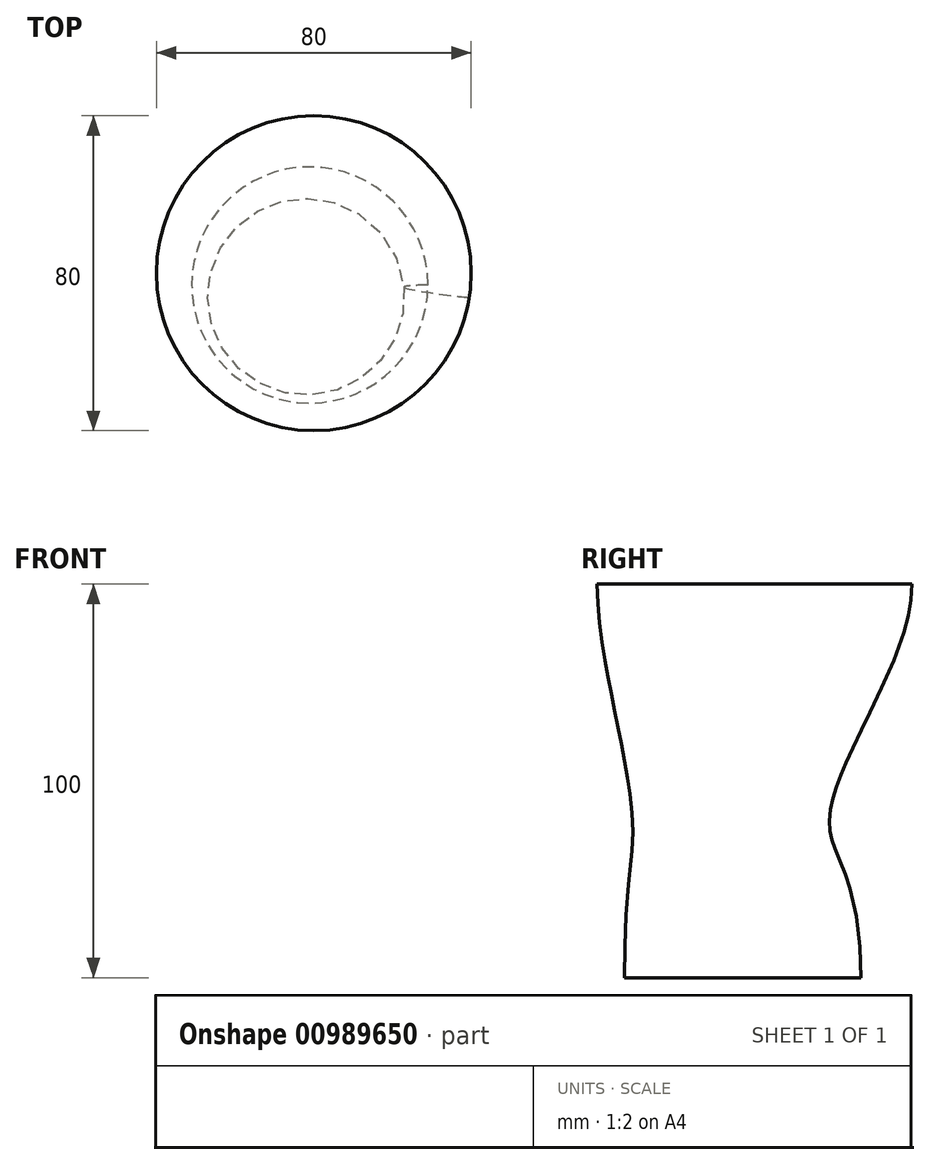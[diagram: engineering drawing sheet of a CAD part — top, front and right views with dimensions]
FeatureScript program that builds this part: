
annotation { "Feature Type Name" : "Feature", "Feature Type Description" : "" }
export const myFeature = defineFeature(function(context is Context, id is Id, definition is map)
    precondition{}
    {
        {
            assignVariable(context, id + "F0", {"name" : "Hossz", "anyValue" : 100});
        }
        {
            var Q0;
            Q0=qCreatedBy(makeId("Top.planeOp"),FACE);
            cPlane(context, id + "F1", {"entities" : qUnion([Q0]), "cplaneType" : CPlaneType.OFFSET, "offset" : (getVariable(context, 'Hossz')) * mm, "width" : 150 * mm, "height" : 150 * mm});
        }
        {
            var Q0;
            Q0=qCreatedBy(makeId("Top.planeOp"),FACE);
            cPlane(context, id + "F2", {"entities" : qUnion([Q0]), "cplaneType" : CPlaneType.OFFSET, "offset" : 40 * mm, "width" : 150 * mm, "height" : 150 * mm});
        }
        {
            var Q0;
            Q0=qCreatedBy(makeId("Top.planeOp"),FACE);
            var sketch = newSketch(context, id + "F3", { "sketchPlane" : qUnion([Q0])});
            skCircle(sketch, "E0", {"center": v(0, 0) * mm, "radius": 30 * mm});
            skSolve(sketch);
        }
        {
            var Q0;
            Q0=qCreatedBy(id+"F2.planeOp",FACE);
            var sketch = newSketch(context, id + "F4", { "sketchPlane" : qUnion([Q0])});
            skCircle(sketch, "E1", {"center": v(-1, -3) * mm, "radius": 25 * mm});
            skSolve(sketch);
        }
        {
            var Q0;
            Q0=qCreatedBy(id+"F1.planeOp",FACE);
            var sketch = newSketch(context, id + "F5", { "sketchPlane" : qUnion([Q0])});
            skCircle(sketch, "E2", {"center": v(1, 3) * mm, "radius": 40 * mm});
            skSolve(sketch);
        }
        {
            var Q0;
            Q0=makeQuery(id+"F3.imprint","IMPRINT",FACE,{"disambiguationData":[TD([[makeQuery(id+"F3.imprint","IMPRINT",EDGE,{"derivedFrom":sQuery(id+"F3.wireOp",EDGE,"E0")}),1.0]])]});
            var Q1;
            Q1=makeQuery(id+"F4.imprint","IMPRINT",FACE,{"disambiguationData":[TD([[makeQuery(id+"F4.imprint","IMPRINT",EDGE,{"derivedFrom":sQuery(id+"F4.wireOp",EDGE,"E1")}),1.0]])]});
            var Q2;
            Q2=makeQuery(id+"F5.imprint","IMPRINT",FACE,{"disambiguationData":[TD([[makeQuery(id+"F5.imprint","IMPRINT",EDGE,{"derivedFrom":sQuery(id+"F5.wireOp",EDGE,"E2")}),1.0]])]});
            loft(context, id + "F6", {"startCondition" : LoftEndDerivativeType.NORMAL_TO_PROFILE, "startMagnitude" : 2, "endCondition" : LoftEndDerivativeType.NORMAL_TO_PROFILE, "endMagnitude" : 1, "sheetProfilesArray" : [{ "sheetProfileEntities" : qUnion([Q0]) }, { "sheetProfileEntities" : qUnion([Q1]) }, { "sheetProfileEntities" : qUnion([Q2]) }]});
        }
    });
